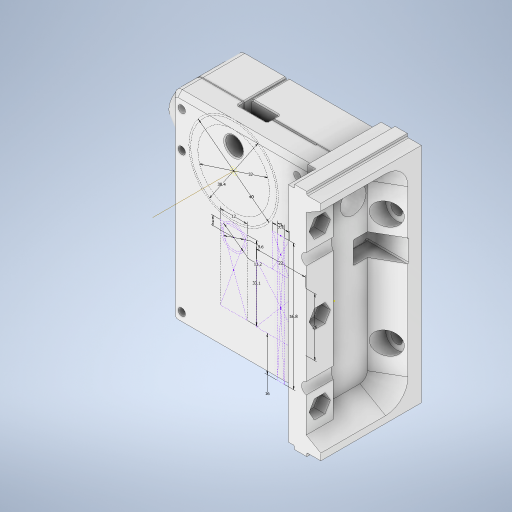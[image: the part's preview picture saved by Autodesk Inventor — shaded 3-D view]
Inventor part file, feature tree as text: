
AUTODESK INVENTOR PART (.ipt)
format: ipt  version: 2024 (Build 280153000, 153)  size: 2,263,552 bytes
history: native  units: mm
features: sketch x40, fillet x31, projected_geometry x28, extrude x27, hole x17, plane x11, other x11, chamfer x7, surface_op x3, thicken_offset x2, mirror x1, revolve x1, split x1
ambient origin geometry x8: Origin, YZ Plane, XZ Plane, XY Plane, X Axis, Y Axis, Z Axis, Center Point
bodies: Solid1 (feature_tree)
feature tree (180):
  extrude  "Extrusion1"  Depth=99.75mm
  extrude  "Extrusion2"  Depth=64.0mm
  plane  "Work Plane2"
  extrude  "Extrusion6"  Depth=30.0mm TaperAngle=0.0deg
  extrude  "Extrusion7"  Depth=13.0mm
  extrude  "Extrusion8"  Depth=54.0mm
  extrude  "Extrusion9"  Depth=16.4mm
  sketch  "Sketch11"  dims[d34=2.37mm d35=0.0mm d36=8.8mm]
  hole  "Hole2"  [1 undecoded]
  hole  "Hole3"  [1 undecoded]
  plane  "Work Plane3"
  plane  "Work Plane5"
  sketch  "Sketch13"  dims[d37=14.8mm d38=0.0mm d39=7.25mm]
  extrude  "Extrusion10"  TaperAngle=180.0deg  [1 undecoded]
  extrude  "Extrusion11"  Depth=4.3mm
  extrude  "Extrusion12"  Depth=7.6mm
  hole  "Hole4"  [1 undecoded]
  extrude  "Extrusion13"  Depth=3.0mm
  plane  "Work Plane6"
  extrude  "Extrusion14"  Depth=12.56mm
  extrude  "Extrusion15"  Depth=5.08mm
  hole  "Hole5"  [1 undecoded]
  extrude  "Extrusion19"  Depth=8.8mm
  extrude  "Extrusion20"  Depth=9.5mm
  extrude  "Extrusion21"  Depth=5.0mm
  extrude  "Extrusion22"  Depth=1.5mm
  fillet  "Fillet3"  Radius=1.5mm
  chamfer  "Chamfer2"  Distance=36.0mm
  hole  "Hole6"  [1 undecoded]
  extrude  "Extrusion23"  Depth=3.0mm
  chamfer  "Chamfer3"  [1 undecoded]
  extrude  "Extrusion24"  Depth=10.0mm
  hole  "Hole7"  [1 undecoded]
  plane  "Work Plane7"
  hole  "Hole8"  [1 undecoded]
  extrude  "Extrusion25"  Depth=5.0mm TaperAngle=30.0deg
  hole  "Hole9"  [1 undecoded]
  chamfer  "Chamfer4"  Distance=6.0mm
  plane  "Work Plane8"
  fillet  "Fillet4"  Radius=6.0mm
  hole  "Hole11"  [1 undecoded]
  hole  "Hole12"  [1 undecoded]
  hole  "Hole13"  [1 undecoded]
  hole  "Hole14"  [1 undecoded]
  hole  "Hole15"  [1 undecoded]
  extrude  "Extrusion26"  Depth=0.75mm TaperAngle=15.0deg
  chamfer  "Chamfer5"  Distance=0.75mm Angle=15.0deg
  chamfer  "Chamfer6"  Distance=3.0mm
  fillet  "Fillet6"  Radius=2.0mm
  chamfer  "Chamfer7"  Distance=0.5mm
  fillet  "Fillet7"  Radius=1.0mm
  fillet  "Fillet9"  Radius=1.0mm
  fillet  "Fillet10"  Radius=0.5mm
  fillet  "Fillet11"  Radius=2.0mm
  fillet  "Fillet14"  Radius=0.5mm
  fillet  "Fillet15"  Radius=1.0mm
  thicken_offset  "Thicken1"
  fillet  "Fillet16"  Radius=3.0mm
  hole  "Hole16"  [1 undecoded]
  sketch  "Sketch44"  dims[d151=5.0mm d152=0.0mm d153=5.0mm d154=2.0mm d155=30.0deg]
  extrude  "Extrusion30"  TaperAngle=150.0deg  [1 undecoded]
  extrude  "Extrusion31"  Depth=10.0mm
  fillet  "Fillet17"  Radius=20.0mm
  plane  "Work Plane9"
  hole  "Hole17"  [1 undecoded]
  plane  "Work Plane10"
  mirror  "Mirror1"
  fillet  "Fillet18"  Radius=0.25mm
  fillet  "Fillet19"  Radius=2.0mm
  fillet  "Fillet20"  Radius=0.25mm
  fillet  "Fillet21"  Radius=0.5mm
  fillet  "Fillet22"  Radius=10.0mm
  fillet  "Fillet23"  Radius=0.5mm
  fillet  "Fillet24"  Radius=0.5mm
  fillet  "Fillet25"  Radius=19.0mm
  hole  "Hole18"  [1 undecoded]
  fillet  "Fillet26"  Radius=3.5mm
  fillet  "Fillet27"  Radius=3.5mm
  fillet  "Fillet28"  Radius=16.0mm
  plane  "Work Plane11"
  revolve  "Revolution1"  [1 undecoded]
  extrude  "Extrusion32"  Depth=0.5mm
  chamfer  "Chamfer8"  Distance=8.0mm
  fillet  "Fillet29"  Radius=6.0mm
  fillet  "Fillet30"  Radius=0.5mm
  fillet  "Fillet32"  [1 undecoded]
  hole  "Hole19"  [1 undecoded]
  fillet  "Fillet33"  Radius=1.0mm
  plane  "Work Plane12"
  sketch  "Sketch54"  dims[d176=5.2mm]
  surface_op  "Trim1"
  fillet  "Fillet36"  Radius=0.5mm
  surface_op  "Stitch Surface1"
  fillet  "Fillet34"  Radius=1.0mm
  split  "Split2"
  thicken_offset  "Thicken3"
  fillet  "Fillet35"  Radius=6.0mm
  extrude  "Extrusion34"  Depth=0.5mm
  fillet  "Fillet37"  Radius=0.5mm
  fillet  "Fillet38"  Radius=0.5mm
  other  "Work Axis4"
  sketch  "Sketch57"  dims[d178=12.0mm d179=6.0mm d180=0.0mm d181=8.35mm d182=6.0mm d183=4.0mm d184=2.0mm d185=90.0deg d186=7.3mm d187=0.0mm d188=6.0mm d189=2.0mm d190=30.0deg d198=4.0mm d199=11.5mm d200=6.0mm d201=4.0mm d202=2.0mm d203=90.0deg d204=8.0mm d205=0.0mm d206=8.35mm d207=6.0mm d208=4.0mm d209=2.0mm d210=90.0deg d211=7.3mm d212=0.0mm d213=4.4mm d214=6.0mm d215=4.0mm d216=2.0mm d217=90.0deg d218=6.0mm d219=0.0mm d220=4.4mm d221=6.0mm d222=4.0mm d223=2.0mm d224=90.0deg d225=15.0mm d226=0.0mm d227=2.0mm d228=6.0mm d229=4.0mm d230=2.0mm d231=90.0deg d232=15.0mm d233=0.0mm d234=10.0mm d235=30.0deg d236=30.0mm d237=0.0mm d238=1.0mm d239=0.75mm d240=2.0mm d241=15.0deg d242=0.75mm d243=2.0mm d244=15.0deg d246=3.0mm d247=2.0mm d248=2.0mm d249=15.0deg d250=0.5mm d252=1.0mm d253=1.0mm d254=0.5mm d257=2.0mm d258=0.5mm d260=1.0mm d261=3.0mm d262=2.0mm d263=150.0deg d264=10.0mm d265=20.0mm d266=6.0mm d267=0.25mm d268=2.0mm d269=0.25mm d270=0.5mm d271=10.0mm d272=0.0mm d273=0.5mm d274=0.5mm d287=19.0mm d288=0.25mm d289=3.5mm d290=3.5mm d291=16.0mm d292=5.7mm d293=5.7mm d294=3.3mm d295=6.0mm d296=4.0mm d297=2.0mm d298=90.0deg d299=6.0mm d300=0.0mm d301=5.7mm d302=8.0mm d303=0.0mm d304=6.0mm d305=0.0mm d306=0.5mm d307=-2.25mm d308=8.75mm d309=6.0mm d310=4.0mm d311=2.0mm d312=90.0deg d313=1.0mm d314=0.0mm d315=0.5mm d316=1.0mm d317=0.5mm d318=1.0mm d319=6.0mm d320=0.0mm d321=0.5mm d322=0.5mm d323=0.5mm d324=0.5mm d325=0.5mm d326=0.5mm d327=5.0mm d328=6.0mm d329=4.0mm d330=2.0mm d331=90.0deg d332=1.0mm d333=0.0mm d334=1.0mm d335=0.5mm d336=0.5mm d338=0.0mm d339=8.2mm d340=45.0deg d341=10.75mm d342=22.5deg d343=45.0deg d344=1.25mm d345=0.0mm d346=1.625mm d347=1.625mm d348=2.0mm d349=45.0deg d350=0.5mm d351=0.25mm d353=0.5mm d361=8.0mm d362=6.0mm d363=4.0mm d364=2.0mm d365=90.0deg d366=8.0mm d367=0.0mm d368=0.5mm d373=0.0mm d374=0.2mm d375=0.2mm d376=0.2mm d377=6.0mm d378=1.0mm d380=0.4mm d381=0.0mm d382=5.0mm d383=0.0mm d384=0.2mm d385=0.4mm d386=1.0mm d387=0.5mm d388=0.5mm d389=0.0mm d390=0.5mm d391=0.5mm d393=40.0mm d394=12.0mm d395=33.1mm d396=4.0mm d397=11.2mm d398=38.4mm d399=9.6mm d400=32.0mm d401=22.0mm d402=26.0mm d403=3.0mm d404=56.8mm d405=16.0mm d406=7.5mm d111=0.5mm d112=0.872665mm d113=0.5mm d114=0.872665mm d352=0.0mm d354=0.0mm d355=0.0mm d392=0.0mm]
  sketch  "Sketch1"  dims[d0=18.0mm d1=99.75mm]
  sketch  "Sketch2"  dims[d2=45.0mm d3=0.0mm d4=64.0mm]
  sketch  "Sketch7"  dims[d5=90.0mm d6=30.0mm d7=0.0mm]
  sketch  "Sketch8"  dims[d27=-7.5mm d28=13.0mm]
  sketch  "Sketch9"  dims[d29=18.0mm d30=54.0mm]
  sketch  "Sketch10"  dims[d31=5.0mm d32=0.0mm d33=16.4mm]
  other  "Work Axis1"
  plane  "Work Plane4"
  sketch  "Sketch15"  dims[d40=0.2mm d41=0.0mm]
  sketch  "Sketch16"  dims[d42=3.2mm d43=6.0mm d44=4.0mm d45=2.0mm d46=90.0deg d47=4.7mm d48=0.0mm]
  sketch  "Sketch17"  dims[d49=3.2mm d50=6.0mm d51=4.0mm d52=2.0mm d53=90.0deg d54=16.3mm d55=0.0mm d59=180.0deg d60=-11.0mm]
  sketch  "Sketch21"  dims[d61=5.1mm d62=4.3mm]
  sketch  "Sketch22"  dims[d63=5.7mm d64=0.0mm d65=7.6mm]
  projected_geometry  "Projected Loop6"
  sketch  "Sketch23"  dims[d66=8.5mm d67=1.5mm d68=0.0mm]
  projected_geometry  "Projected Loop7"
  sketch  "Sketch24"  dims[d69=11.2mm d70=3.0mm]
  projected_geometry  "Projected Loop8"
  sketch  "Sketch25"  dims[d72=19.0mm d73=0.0mm d74=12.56mm]
  projected_geometry  "Projected Loop9"
  sketch  "Sketch26"  dims[d75=1.75mm d76=6.0mm d77=4.0mm d78=2.0mm d79=90.0deg d80=9.0mm d81=20.594885mm d82=5.08mm]
  projected_geometry  "Projected Loop10"
  sketch  "Sketch27"  dims[d83=2.0mm d84=13.75mm]
  projected_geometry  "Projected Loop11"
  sketch  "Sketch28"  dims[d85=2.5mm d86=0.0mm d88=8.8mm]
  projected_geometry  "Projected Loop12"
  sketch  "Sketch29"  dims[d89=13.0mm d90=9.5mm]
  sketch  "Sketch30"  dims[d91=5.25mm d92=0.0mm d93=5.0mm]
  sketch  "Sketch31"  dims[d94=0.5mm d95=0.0mm]
  sketch  "Sketch33"  dims[d96=3.3mm d97=6.0mm d98=4.0mm d99=2.0mm d100=90.0deg d101=9.0mm d102=20.594885mm d123=5.5mm d124=1.5mm d125=36.0mm d126=0.0mm]
  projected_geometry  "Projected Loop13"
  sketch  "Sketch34"  dims[d127=12.25mm d128=3.5mm d129=0.0mm]
  sketch  "Sketch35"  dims[d130=3.0mm d131=3.0mm]
  sketch  "Sketch36"  dims[d132=3.0mm d133=0.0mm d134=0.0mm]
  sketch  "Sketch37"  dims[d135=6.0mm d136=0.0mm d137=10.0mm]
  sketch  "Sketch38"  dims[d138=11.5mm d139=2.0mm d140=30.0deg d141=70.0mm]
  sketch  "Sketch39"  dims[d142=6.0mm]
  projected_geometry  "Projected Loop14"
  projected_geometry  "Projected Loop15"
  other  "Srf1"
  sketch  "Sketch43"  dims[d143=5.3mm d144=6.0mm d145=4.0mm d146=2.0mm d147=90.0deg d148=8.0mm d149=20.594885mm d150=12.0mm]
  projected_geometry  "Projected Loop32"
  projected_geometry  "Projected Loop33"
  projected_geometry  "Projected Loop34"
  projected_geometry  "Projected Loop35"
  projected_geometry  "Projected Loop36"
  sketch  "Sketch45"  dims[d156=8.25mm d157=5.0mm d158=0.0mm]
  sketch  "Sketch46"  dims[d159=50.0mm]
  other  "Srf2"
  sketch  "Sketch47"  dims[d160=5.3mm d161=6.0mm d162=4.0mm d163=2.0mm d164=90.0deg d165=8.0mm d166=20.594885mm]
  other  "Work Axis2"
  other  "Work Axis3"
  sketch  "Sketch48"  dims[d167=-5.0mm]
  projected_geometry  "Projected Loop37"
  sketch  "Sketch49"  dims[d168=10.0mm d169=6.0mm d170=4.0mm d171=2.0mm d172=90.0deg d173=8.0mm d174=20.594885mm]
  projected_geometry  "Projected Loop38"
  sketch  "Sketch52"  dims[d175=2.2mm]
  other  "Srf5"
  other  "Srf6"
  other  "Srf7"
  sketch  "Sketch55"  dims[d177=8.6mm]
  projected_geometry  "Projected Loop42"
  extrude  "ExtrusionSrf1"  Depth=0.5mm
  extrude  "ExtrusionSrf2"  Depth=0.5mm
  extrude  "ExtrusionSrf4"  Depth=0.5mm
  surface_op  "Boundary Patch1"
  projected_geometry  "Project Cut Edges2"
  projected_geometry  "Project Cut Edges3"
  projected_geometry  "Project Cut Edges4"
  projected_geometry  "Project Cut Edges5"
  projected_geometry  "Project Cut Edges6"
  projected_geometry  "Project Cut Edges7"
  projected_geometry  "Project Cut Edges8"
  projected_geometry  "Project Cut Edges11"
  projected_geometry  "Project Cut Edges12"
  projected_geometry  "Project Cut Edges13"
  other  "Filament Motion Sensor Base"
  other  "Filmament Motion Sensor Cap"
note: 22 required parameter values undecoded (feature->parameter linkage not recoverable at this tier; creation-order binding heuristic only, values carry confidence <= 0.55)